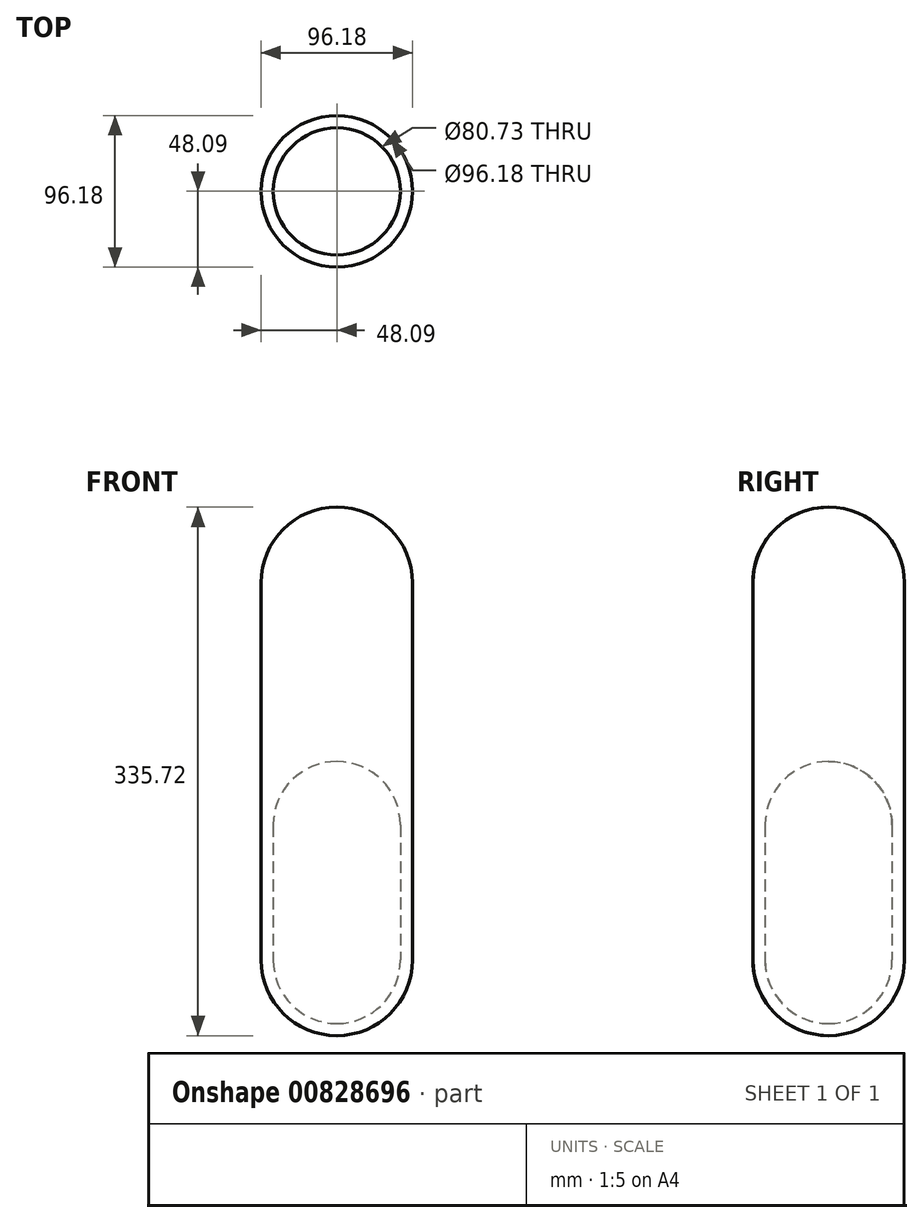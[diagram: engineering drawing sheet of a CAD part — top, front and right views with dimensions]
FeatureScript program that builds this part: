
annotation { "Feature Type Name" : "Feature", "Feature Type Description" : "" }
export const myFeature = defineFeature(function(context is Context, id is Id, definition is map)
    precondition{}
    {
        {
            var Q0;
            Q0=qCreatedBy(makeId("Right.planeOp"),FACE);
            var sketch = newSketch(context, id + "F0", { "sketchPlane" : qUnion([Q0])});
            skArc(sketch, "E0", {"start": v(-40.37, 0) * mm, "mid": v(-28.54, -28.54) * mm, "end": v(0, -40.37) * mm});
            skArc(sketch, "E1", {"start": v(-40.37, 85.69) * mm, "mid": v(-28.54, 114.23) * mm, "end": v(0, 126.05) * mm});
            skLineSegment(sketch, "E2", {"start": v(0, -40.37) * mm, "end": v(0, -48.09) * mm});
            skArc(sketch, "E3", {"start": v(0, -48.09) * mm, "mid": v(-34, -34) * mm, "end": v(-48.09, 0) * mm});
            skLineSegment(sketch, "E4", {"start": v(-48.09, 0) * mm, "end": v(-48.09, 85.69) * mm});
            skLineSegment(sketch, "E5", {"start": v(-48.09, 85.69) * mm, "end": v(-48.09, 239.54) * mm});
            skLineSegment(sketch, "E6", {"start": v(-40.37, 0) * mm, "end": v(-40.37, 72.91) * mm});
            skArc(sketch, "E7", {"start": v(-48.09, 239.54) * mm, "mid": v(-34, 273.54) * mm, "end": v(0, 287.63) * mm});
            skLineSegment(sketch, "E8", {"start": v(-40.37, 85.69) * mm, "end": v(-40.37, 72.91) * mm});
            skSolve(sketch);
        }
        {
            var Q0;
            Q0=qCreatedBy(makeId("Right.planeOp"),FACE);
            var sketch = newSketch(context, id + "F1", { "sketchPlane" : qUnion([Q0])});
            skLineSegment(sketch, "E9", {"start": v(0, 325.2) * mm, "end": v(0, -113.97) * mm, "construction": true});
            skSolve(sketch);
        }
        {
            var Q0;
            Q0 = qSketchRegion(id + "F0", true);
            var Q1;
            Q1=sQuery(id+"F0.wireOp",EDGE,"E7");
            var Q2;
            Q2=sQuery(id+"F0.wireOp",EDGE,"E5");
            var Q3;
            Q3=sQuery(id+"F0.wireOp",EDGE,"E1");
            var Q4;
            Q4=sQuery(id+"F0.wireOp",EDGE,"E4");
            var Q5;
            Q5=sQuery(id+"F0.wireOp",EDGE,"E6");
            var Q6;
            Q6=sQuery(id+"F0.wireOp",EDGE,"E8");
            var Q7;
            Q7=sQuery(id+"F0.wireOp",EDGE,"E3");
            var Q8;
            Q8=sQuery(id+"F0.wireOp",EDGE,"E0");
            var Q9;
            Q9=sQuery(id+"F1.wireOp",EDGE,"E9");
            revolve(context, id + "F2", {"bodyType" : ToolBodyType.SURFACE, "surfaceOperationType" : NewSurfaceOperationType.NEW, "entities" : qUnion([Q0]), "surfaceEntities" : qUnion([Q1, Q2, Q3, Q4, Q5, Q6, Q7, Q8]), "axis" : qUnion([Q9]), "revolveType" : RevolveType.FULL});
        }
    });
